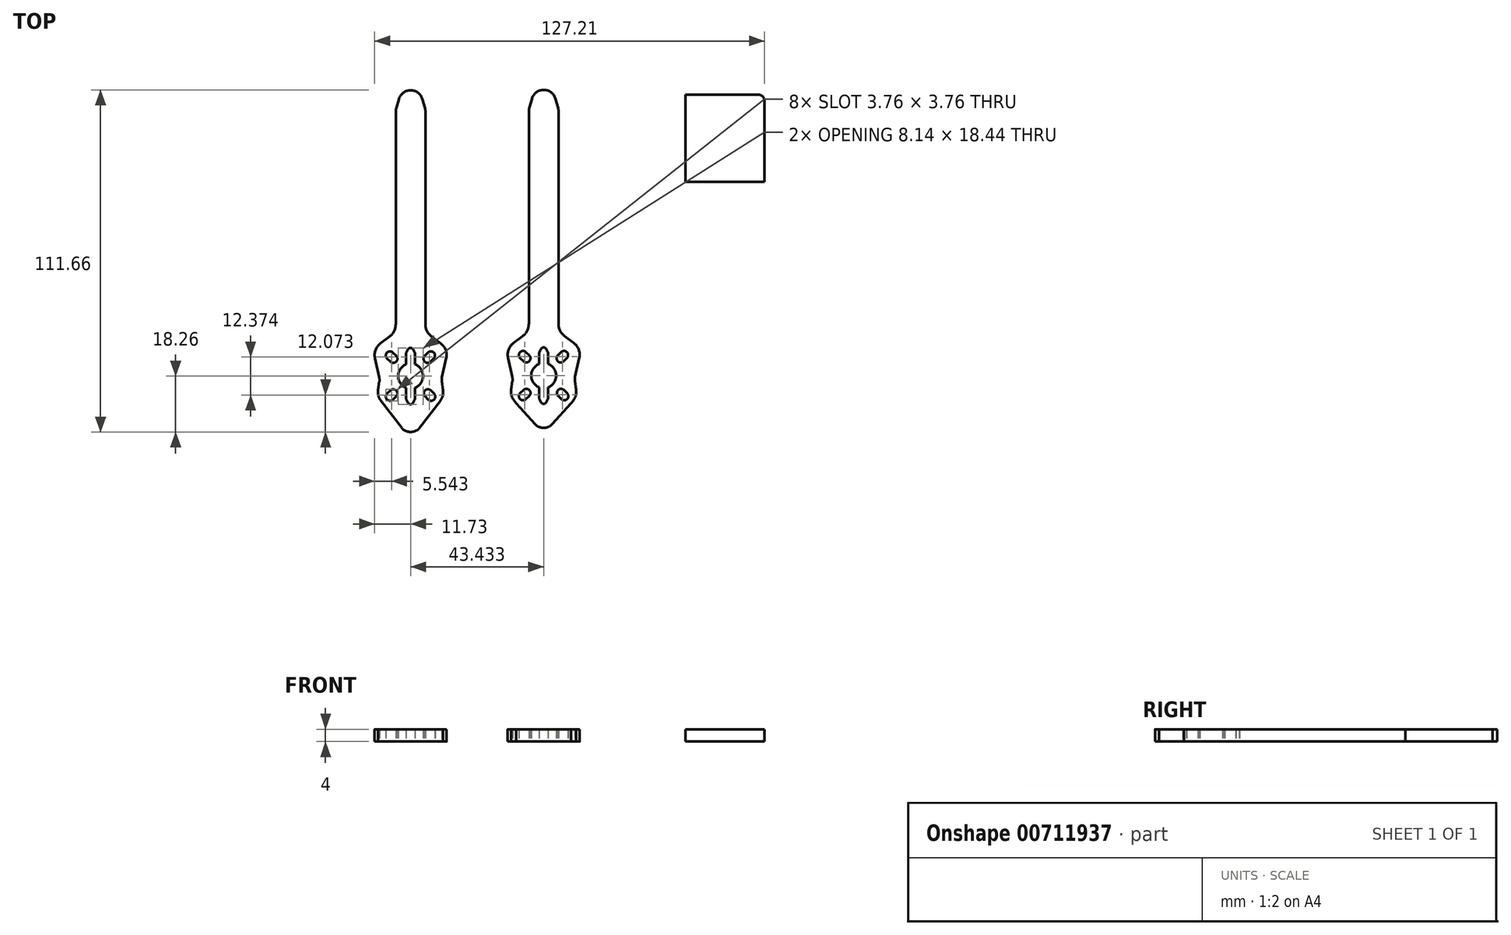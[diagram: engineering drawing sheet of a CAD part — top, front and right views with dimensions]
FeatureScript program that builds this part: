
annotation { "Feature Type Name" : "Feature", "Feature Type Description" : "" }
export const myFeature = defineFeature(function(context is Context, id is Id, definition is map)
    precondition{}
    {
        {
            var Q0;
            Q0=qCreatedBy(makeId("Top.planeOp"),FACE);
            var sketch = newSketch(context, id + "F0", { "sketchPlane" : qUnion([Q0])});
            skLineSegment(sketch, "E0", {"start": v(-0.1, -45.8) * mm, "end": v(-0.1, -63.2) * mm, "construction": true});
            skLineSegment(sketch, "E1", {"start": v(-0.1, -45.8) * mm, "end": v(-15.07, -60.77) * mm, "construction": true});
            skArc(sketch, "E2", {"start": v(-6.71, -41.1) * mm, "mid": v(-4.8, -41.1) * mm, "end": v(-4.8, -39.19) * mm});
            skArc(sketch, "E3", {"start": v(-5.86, -38.13) * mm, "mid": v(-7.77, -38.13) * mm, "end": v(-7.77, -40.04) * mm});
            skLineSegment(sketch, "E4", {"start": v(-4.8, -39.19) * mm, "end": v(-5.86, -38.13) * mm});
            skLineSegment(sketch, "E5.MirrorCS", {"start": v(-6.71, -41.1) * mm, "end": v(-7.77, -40.04) * mm});
            skLineSegment(sketch, "E6.MirrorCS", {"start": v(6.41, -41.1) * mm, "end": v(7.47, -40.04) * mm});
            skArc(sketch, "E7.MirrorCS", {"start": v(5.56, -38.13) * mm, "mid": v(7.47, -38.13) * mm, "end": v(7.47, -40.04) * mm});
            skLineSegment(sketch, "E8.MirrorCS", {"start": v(4.5, -39.19) * mm, "end": v(5.56, -38.13) * mm});
            skArc(sketch, "E9.MirrorCS", {"start": v(6.41, -41.1) * mm, "mid": v(4.5, -41.1) * mm, "end": v(4.5, -39.19) * mm});
            skLineSegment(sketch, "E10.MirrorCS", {"start": v(4.6, -52.41) * mm, "end": v(5.66, -53.47) * mm});
            skLineSegment(sketch, "E11.MirrorCS", {"start": v(6.51, -50.5) * mm, "end": v(7.57, -51.56) * mm});
            skArc(sketch, "E12.MirrorCS", {"start": v(6.51, -50.5) * mm, "mid": v(4.6, -50.5) * mm, "end": v(4.6, -52.41) * mm});
            skArc(sketch, "E13.MirrorCS", {"start": v(5.66, -53.47) * mm, "mid": v(7.57, -53.47) * mm, "end": v(7.57, -51.56) * mm});
            skLineSegment(sketch, "E14.MirrorCS", {"start": v(-4.8, -52.41) * mm, "end": v(-5.86, -53.47) * mm});
            skLineSegment(sketch, "E15.MirrorCS", {"start": v(-6.71, -50.5) * mm, "end": v(-7.77, -51.56) * mm});
            skArc(sketch, "E16.MirrorCS", {"start": v(-5.86, -53.47) * mm, "mid": v(-7.77, -53.47) * mm, "end": v(-7.77, -51.56) * mm});
            skArc(sketch, "E17.MirrorCS", {"start": v(-6.71, -50.5) * mm, "mid": v(-4.8, -50.5) * mm, "end": v(-4.8, -52.41) * mm});
            skLineSegment(sketch, "E18.left", {"start": v(1.4, -52.78) * mm, "end": v(1.4, -49.59) * mm});
            skLineSegment(sketch, "E18.right", {"start": v(-1.6, -52.78) * mm, "end": v(-1.6, -49.59) * mm});
            skLineSegment(sketch, "E19.trimOffspring", {"start": v(-1.6, -42.01) * mm, "end": v(-1.6, -38.82) * mm});
            skLineSegment(sketch, "E20.trimOffspring", {"start": v(1.4, -42.01) * mm, "end": v(1.4, -38.82) * mm});
            skArc(sketch, "E21.MirrorCS", {"start": v(-1.35, -37.85) * mm, "mid": v(-1.54, -38.32) * mm, "end": v(-1.6, -38.82) * mm});
            skArc(sketch, "E22.MirrorCS", {"start": v(1.4, -38.82) * mm, "mid": v(1.34, -38.32) * mm, "end": v(1.15, -37.85) * mm});
            skArc(sketch, "E23.MirrorCS", {"start": v(1.4, -52.78) * mm, "mid": v(1.34, -53.28) * mm, "end": v(1.15, -53.75) * mm});
            skArc(sketch, "E24.MirrorCS", {"start": v(-1.35, -53.75) * mm, "mid": v(-1.54, -53.28) * mm, "end": v(-1.6, -52.78) * mm});
            skCircle(sketch, "E25", {"center": v(-0.1, -45.8) * mm, "radius": 8 * mm, "construction": true});
            skLineSegment(sketch, "E26.MirrorCS", {"start": v(1.15, -37.85) * mm, "end": v(0.71, -37.06) * mm});
            skLineSegment(sketch, "E27.MirrorCS", {"start": v(-1.35, -37.85) * mm, "end": v(-0.91, -37.06) * mm});
            skArc(sketch, "E28.MirrorCS", {"start": v(-0.91, -37.06) * mm, "mid": v(-0.1, -36.58) * mm, "end": v(0.71, -37.06) * mm});
            skPoint(sketch, "E29.MirrorCS.start.orphan", {"position": v(-8.6, -37.25) * mm});
            skPoint(sketch, "E30.visualSharp", {"position": v(4.9, -63.2) * mm});
            skPoint(sketch, "E31.orphan", {"position": v(3.27, -64.64) * mm});
            skPoint(sketch, "E32", {"position": v(-0.1, -34.38) * mm});
            skPoint(sketch, "E33", {"position": v(-0.1, -36.58) * mm});
            skPoint(sketch, "E34", {"position": v(-0.1, -36.3) * mm});
            skArc(sketch, "E35", {"start": v(1.4, -49.59) * mm, "mid": v(3.97, -45.8) * mm, "end": v(1.4, -42.01) * mm});
            skArc(sketch, "E36.trimOffspring", {"start": v(-1.6, -42.01) * mm, "mid": v(-4.17, -45.8) * mm, "end": v(-1.6, -49.59) * mm});
            skPoint(sketch, "E37.MirrorP", {"position": v(-4.93, -29.8) * mm});
            skPoint(sketch, "E38.orphan", {"position": v(-8.46, -56.94) * mm});
            skPoint(sketch, "E39.visualSharp", {"position": v(-0.1, -65.3) * mm});
            skPoint(sketch, "E40.start.orphan", {"position": v(-2.37, -63.85) * mm});
            skPoint(sketch, "E41.orphan", {"position": v(2.17, -63.85) * mm});
            skPoint(sketch, "E42.orphan", {"position": v(6.78, -32.2) * mm});
            skPoint(sketch, "E43.MirrorCS.start.orphan", {"position": v(9.23, -33.3) * mm});
            skLineSegment(sketch, "E44", {"start": v(-0.1, -45.8) * mm, "end": v(1.26, -45.8) * mm, "construction": true});
            skLineSegment(sketch, "E45.MirrorCS", {"start": v(1.15, -53.75) * mm, "end": v(0.71, -54.54) * mm});
            skLineSegment(sketch, "E46.MirrorCS", {"start": v(-1.35, -53.75) * mm, "end": v(-0.91, -54.54) * mm});
            skArc(sketch, "E47.MirrorCS", {"start": v(-0.91, -54.54) * mm, "mid": v(-0.1, -55.02) * mm, "end": v(0.71, -54.54) * mm});
            skPoint(sketch, "E48.MirrorP", {"position": v(-12.53, -37.52) * mm});
            skLineSegment(sketch, "E49.MirrorCS", {"start": v(-9.87, -53.74) * mm, "end": v(-9.08, -54.78) * mm});
            skPoint(sketch, "E50.MirrorP", {"position": v(-9.3, -54.73) * mm});
            skLineSegment(sketch, "E51.MirrorCS", {"start": v(-10.67, -50.39) * mm, "end": v(-10.28, -47.6) * mm});
            skPoint(sketch, "E52.MirrorP", {"position": v(-11.56, -41.04) * mm});
            skPoint(sketch, "E53.MirrorP", {"position": v(-9.43, -33.3) * mm});
            skPoint(sketch, "E54.MirrorP", {"position": v(-8.6, -38.35) * mm});
            skPoint(sketch, "E55.MirrorP", {"position": v(-11.15, -41.7) * mm});
            skPoint(sketch, "E56.MirrorP", {"position": v(-10.73, -48.92) * mm});
            skLineSegment(sketch, "E57", {"start": v(-4.93, -28.16) * mm, "end": v(-4.93, -28.9) * mm});
            skPoint(sketch, "E58.end.orphan", {"position": v(-6.38, -32.73) * mm});
            skPoint(sketch, "E59.MirrorCS.end.orphan", {"position": v(6.18, -32.73) * mm});
            skPoint(sketch, "E60.visualSharp", {"position": v(-4.93, -31.43) * mm});
            skArc(sketch, "E60.filletArc", {"start": v(-6.98, -32.93) * mm, "mid": v(-5.47, -31.16) * mm, "end": v(-4.93, -28.9) * mm});
            skPoint(sketch, "E61.MirrorCS.end.orphan", {"position": v(-6.98, -32.2) * mm});
            skPoint(sketch, "E62.MirrorCS.end.orphan", {"position": v(4.73, -31.43) * mm});
            skArc(sketch, "E63.MirrorCS", {"start": v(6.78, -32.93) * mm, "mid": v(5.27, -31.16) * mm, "end": v(4.73, -28.9) * mm});
            skLineSegment(sketch, "E64.MirrorCS", {"start": v(4.73, -28.16) * mm, "end": v(4.73, -28.9) * mm});
            skLineSegment(sketch, "E65", {"start": v(-9.08, -54.78) * mm, "end": v(-2.91, -62.86) * mm});
            skArc(sketch, "E66", {"start": v(-2.52, -63.26) * mm, "mid": v(-0.1, -64.06) * mm, "end": v(2.32, -63.26) * mm});
            skPoint(sketch, "E67.orphan", {"position": v(-2.64, -63.23) * mm});
            skPoint(sketch, "E68.orphan", {"position": v(2.44, -63.23) * mm});
            skPoint(sketch, "E69.visualSharp", {"position": v(-2.77, -63.05) * mm});
            skArc(sketch, "E69.filletArc", {"start": v(-2.91, -62.86) * mm, "mid": v(-2.73, -63.07) * mm, "end": v(-2.52, -63.26) * mm});
            skPoint(sketch, "E70.visualSharp", {"position": v(2.57, -63.05) * mm});
            skArc(sketch, "E70.filletArc", {"start": v(2.32, -63.26) * mm, "mid": v(2.53, -63.07) * mm, "end": v(2.71, -62.86) * mm});
            skPoint(sketch, "E71.visualSharp", {"position": v(-12.78, -36.79) * mm});
            skLineSegment(sketch, "E72", {"start": v(-9.94, -35.14) * mm, "end": v(-6.98, -32.93) * mm});
            skLineSegment(sketch, "E73.MirrorCS", {"start": v(9.74, -35.14) * mm, "end": v(6.78, -32.93) * mm});
            skLineSegment(sketch, "E74", {"start": v(-4.93, -28.16) * mm, "end": v(-4.93, -23.9) * mm});
            skLineSegment(sketch, "E75.MirrorCS", {"start": v(4.73, -28.16) * mm, "end": v(4.73, -23.9) * mm});
            skLineSegment(sketch, "E76", {"start": v(-4.93, -23.9) * mm, "end": v(-4.93, 40.52) * mm});
            skLineSegment(sketch, "E77", {"start": v(4.73, -23.9) * mm, "end": v(4.73, 40.54) * mm});
            skLineSegment(sketch, "E78", {"start": v(4.59, 41.62) * mm, "end": v(3.77, 44.53) * mm});
            skLineSegment(sketch, "E79", {"start": v(-3.92, 44.58) * mm, "end": v(-4.77, 41.64) * mm});
            skPoint(sketch, "E80.visualSharp", {"position": v(0, 58.06) * mm});
            skArc(sketch, "E80.filletArc", {"start": v(3.77, 44.53) * mm, "mid": v(-0.06, 47.46) * mm, "end": v(-3.92, 44.58) * mm});
            skPoint(sketch, "E81.visualSharp", {"position": v(4.73, 41.1) * mm});
            skArc(sketch, "E81.filletArc", {"start": v(4.73, 40.54) * mm, "mid": v(4.7, 41.09) * mm, "end": v(4.59, 41.62) * mm});
            skPoint(sketch, "E82.visualSharp", {"position": v(-4.93, 41.1) * mm});
            skArc(sketch, "E82.filletArc", {"start": v(-4.77, 41.64) * mm, "mid": v(-4.9, 41.09) * mm, "end": v(-4.93, 40.52) * mm});
            skPoint(sketch, "E83", {"position": v(-10.67, -50.39) * mm});
            skPoint(sketch, "E84.visualSharp", {"position": v(-10.48, -52.95) * mm});
            skPoint(sketch, "E85", {"position": v(-10.18, -46.9) * mm});
            skPoint(sketch, "E86.MirrorCS.end.orphan", {"position": v(-10.04, -45.83) * mm});
            skPoint(sketch, "E86.MirrorCS.start.orphan", {"position": v(-10.17, -44.45) * mm});
            skPoint(sketch, "E87.start.orphan", {"position": v(-11.5, -40.54) * mm});
            skArc(sketch, "E88.filletArc", {"start": v(-10.28, -47.6) * mm, "mid": v(-10.25, -46.9) * mm, "end": v(-10.34, -46.2) * mm});
            skLineSegment(sketch, "E89.MirrorCS", {"start": v(8.88, -54.78) * mm, "end": v(2.71, -62.86) * mm});
            skArc(sketch, "E90.MirrorCS", {"start": v(10.08, -47.6) * mm, "mid": v(10.05, -46.9) * mm, "end": v(10.14, -46.2) * mm});
            skLineSegment(sketch, "E91.MirrorCS", {"start": v(11.52, -39.9) * mm, "end": v(10.14, -46.2) * mm});
            skArc(sketch, "E92", {"start": v(11.52, -39.9) * mm, "mid": v(11.33, -37.26) * mm, "end": v(9.74, -35.14) * mm});
            skPoint(sketch, "E71.filletArc.end.orphan", {"position": v(-11.72, -39.9) * mm});
            skArc(sketch, "E93.MirrorCS", {"start": v(-11.72, -39.9) * mm, "mid": v(-11.53, -37.26) * mm, "end": v(-9.94, -35.14) * mm});
            skLineSegment(sketch, "E94.MirrorCS", {"start": v(-11.72, -39.9) * mm, "end": v(-10.34, -46.2) * mm});
            skArc(sketch, "E95", {"start": v(-10.67, -50.39) * mm, "mid": v(-10.71, -51.37) * mm, "end": v(-10.56, -52.33) * mm});
            skPoint(sketch, "E96.visualSharp", {"position": v(-10.16, -53.36) * mm});
            skArc(sketch, "E96.filletArc", {"start": v(-10.56, -52.33) * mm, "mid": v(-10.28, -53.07) * mm, "end": v(-9.87, -53.74) * mm});
            skPoint(sketch, "E97.MirrorCS.end.orphan", {"position": v(8.88, -54.78) * mm});
            skArc(sketch, "E98.MirrorCS", {"start": v(10.36, -52.33) * mm, "mid": v(10.08, -53.07) * mm, "end": v(9.67, -53.74) * mm});
            skPoint(sketch, "E99.MirrorP", {"position": v(9.1, -54.73) * mm});
            skPoint(sketch, "E100.MirrorP", {"position": v(10.47, -50.39) * mm});
            skPoint(sketch, "E101.MirrorP", {"position": v(10.28, -52.95) * mm});
            skPoint(sketch, "E102.MirrorP", {"position": v(9.96, -53.36) * mm});
            skPoint(sketch, "E103.MirrorP", {"position": v(10.53, -48.92) * mm});
            skArc(sketch, "E104.MirrorCS", {"start": v(10.47, -50.39) * mm, "mid": v(10.51, -51.37) * mm, "end": v(10.36, -52.33) * mm});
            skLineSegment(sketch, "E105.MirrorCS", {"start": v(10.47, -50.39) * mm, "end": v(10.08, -47.6) * mm});
            skLineSegment(sketch, "E106.MirrorCS", {"start": v(9.67, -53.74) * mm, "end": v(8.88, -54.78) * mm});
            skLineSegment(sketch, "E107", {"start": v(-9.08, -54.78) * mm, "end": v(-2.87, -61.64) * mm});
            skLineSegment(sketch, "E108.MirrorCS", {"start": v(8.88, -54.78) * mm, "end": v(2.67, -61.64) * mm});
            skArc(sketch, "E109", {"start": v(-2.87, -61.64) * mm, "mid": v(-0.1, -62.86) * mm, "end": v(2.67, -61.64) * mm});
            skLineSegment(sketch, "E110", {"start": v(43.33, -45.66) * mm, "end": v(43.33, -63.05) * mm, "construction": true});
            skLineSegment(sketch, "E111", {"start": v(43.33, -45.66) * mm, "end": v(28.36, -60.63) * mm, "construction": true});
            skArc(sketch, "E112", {"start": v(36.72, -40.96) * mm, "mid": v(38.63, -40.96) * mm, "end": v(38.63, -39.05) * mm});
            skArc(sketch, "E113", {"start": v(37.57, -37.99) * mm, "mid": v(35.66, -37.99) * mm, "end": v(35.66, -39.9) * mm});
            skLineSegment(sketch, "E114", {"start": v(38.63, -39.05) * mm, "end": v(37.57, -37.99) * mm});
            skLineSegment(sketch, "E115.MirrorCS", {"start": v(36.72, -40.96) * mm, "end": v(35.66, -39.9) * mm});
            skLineSegment(sketch, "E116.MirrorCS", {"start": v(49.84, -40.96) * mm, "end": v(50.9, -39.9) * mm});
            skArc(sketch, "E117.MirrorCS", {"start": v(49, -37.99) * mm, "mid": v(50.9, -37.99) * mm, "end": v(50.9, -39.9) * mm});
            skLineSegment(sketch, "E118.MirrorCS", {"start": v(47.93, -39.05) * mm, "end": v(49, -37.99) * mm});
            skArc(sketch, "E119.MirrorCS", {"start": v(49.84, -40.96) * mm, "mid": v(47.93, -40.96) * mm, "end": v(47.93, -39.05) * mm});
            skLineSegment(sketch, "E120.MirrorCS", {"start": v(48.04, -52.27) * mm, "end": v(49.1, -53.33) * mm});
            skLineSegment(sketch, "E121.MirrorCS", {"start": v(49.94, -50.36) * mm, "end": v(51, -51.42) * mm});
            skArc(sketch, "E122.MirrorCS", {"start": v(49.94, -50.36) * mm, "mid": v(48.04, -50.36) * mm, "end": v(48.04, -52.27) * mm});
            skArc(sketch, "E123.MirrorCS", {"start": v(49.1, -53.33) * mm, "mid": v(51, -53.33) * mm, "end": v(51, -51.42) * mm});
            skLineSegment(sketch, "E124.MirrorCS", {"start": v(38.63, -52.27) * mm, "end": v(37.57, -53.33) * mm});
            skLineSegment(sketch, "E125.MirrorCS", {"start": v(36.72, -50.36) * mm, "end": v(35.66, -51.42) * mm});
            skArc(sketch, "E126.MirrorCS", {"start": v(37.57, -53.33) * mm, "mid": v(35.66, -53.33) * mm, "end": v(35.66, -51.42) * mm});
            skArc(sketch, "E127.MirrorCS", {"start": v(36.72, -50.36) * mm, "mid": v(38.63, -50.36) * mm, "end": v(38.63, -52.27) * mm});
            skLineSegment(sketch, "E128.left", {"start": v(44.83, -52.64) * mm, "end": v(44.83, -49.44) * mm});
            skLineSegment(sketch, "E128.right", {"start": v(41.83, -52.64) * mm, "end": v(41.83, -49.44) * mm});
            skLineSegment(sketch, "E129.trimOffspring", {"start": v(41.83, -41.87) * mm, "end": v(41.83, -38.68) * mm});
            skLineSegment(sketch, "E130.trimOffspring", {"start": v(44.83, -41.87) * mm, "end": v(44.83, -38.68) * mm});
            skArc(sketch, "E131.MirrorCS", {"start": v(42.08, -37.7) * mm, "mid": v(41.9, -38.17) * mm, "end": v(41.83, -38.68) * mm});
            skArc(sketch, "E132.MirrorCS", {"start": v(44.83, -38.68) * mm, "mid": v(44.77, -38.17) * mm, "end": v(44.58, -37.7) * mm});
            skArc(sketch, "E133.MirrorCS", {"start": v(44.83, -52.64) * mm, "mid": v(44.77, -53.14) * mm, "end": v(44.58, -53.61) * mm});
            skArc(sketch, "E134.MirrorCS", {"start": v(42.08, -53.61) * mm, "mid": v(41.9, -53.14) * mm, "end": v(41.83, -52.64) * mm});
            skCircle(sketch, "E135", {"center": v(43.33, -45.66) * mm, "radius": 8 * mm, "construction": true});
            skLineSegment(sketch, "E136.MirrorCS", {"start": v(44.58, -37.7) * mm, "end": v(44.15, -36.92) * mm});
            skLineSegment(sketch, "E137.MirrorCS", {"start": v(42.08, -37.7) * mm, "end": v(42.52, -36.92) * mm});
            skArc(sketch, "E138.MirrorCS", {"start": v(42.52, -36.92) * mm, "mid": v(43.33, -36.44) * mm, "end": v(44.15, -36.92) * mm});
            skPoint(sketch, "E139.MirrorCS.start.orphan", {"position": v(34.83, -37.11) * mm});
            skPoint(sketch, "E140.orphan", {"position": v(46.7, -64.5) * mm});
            skPoint(sketch, "E141", {"position": v(43.33, -34.24) * mm});
            skPoint(sketch, "E142", {"position": v(43.33, -36.44) * mm});
            skPoint(sketch, "E143", {"position": v(43.33, -36.16) * mm});
            skArc(sketch, "E144", {"start": v(44.83, -49.44) * mm, "mid": v(47.4, -45.66) * mm, "end": v(44.83, -41.87) * mm});
            skArc(sketch, "E145.trimOffspring", {"start": v(41.83, -41.87) * mm, "mid": v(39.26, -45.66) * mm, "end": v(41.83, -49.44) * mm});
            skPoint(sketch, "E146.MirrorP", {"position": v(38.5, -29.66) * mm});
            skPoint(sketch, "E147.orphan", {"position": v(34.98, -56.8) * mm});
            skPoint(sketch, "E148.visualSharp", {"position": v(43.33, -65.15) * mm});
            skPoint(sketch, "E149.orphan", {"position": v(50.22, -32.05) * mm});
            skPoint(sketch, "E150.MirrorCS.start.orphan", {"position": v(52.66, -33.17) * mm});
            skLineSegment(sketch, "E151", {"start": v(43.33, -45.66) * mm, "end": v(44.7, -45.66) * mm, "construction": true});
            skLineSegment(sketch, "E152.MirrorCS", {"start": v(44.58, -53.61) * mm, "end": v(44.15, -54.4) * mm});
            skLineSegment(sketch, "E153.MirrorCS", {"start": v(42.08, -53.61) * mm, "end": v(42.52, -54.4) * mm});
            skArc(sketch, "E154.MirrorCS", {"start": v(42.52, -54.4) * mm, "mid": v(43.33, -54.88) * mm, "end": v(44.15, -54.4) * mm});
            skPoint(sketch, "E155.MirrorP", {"position": v(30.9, -37.38) * mm});
            skLineSegment(sketch, "E156.MirrorCS", {"start": v(33.56, -53.6) * mm, "end": v(34.35, -54.64) * mm});
            skPoint(sketch, "E157.MirrorP", {"position": v(34.13, -54.59) * mm});
            skLineSegment(sketch, "E158.MirrorCS", {"start": v(32.76, -50.25) * mm, "end": v(33.15, -47.47) * mm});
            skPoint(sketch, "E159.MirrorP", {"position": v(31.87, -40.9) * mm});
            skPoint(sketch, "E160.MirrorP", {"position": v(34, -33.17) * mm});
            skPoint(sketch, "E161.MirrorP", {"position": v(34.83, -38.21) * mm});
            skPoint(sketch, "E162.MirrorP", {"position": v(32.28, -41.56) * mm});
            skPoint(sketch, "E163.MirrorP", {"position": v(32.7, -48.77) * mm});
            skLineSegment(sketch, "E164", {"start": v(38.5, -28.02) * mm, "end": v(38.5, -28.76) * mm});
            skPoint(sketch, "E165.end.orphan", {"position": v(37.05, -32.6) * mm});
            skPoint(sketch, "E166.MirrorCS.end.orphan", {"position": v(49.61, -32.6) * mm});
            skPoint(sketch, "E167.visualSharp", {"position": v(38.5, -31.3) * mm});
            skArc(sketch, "E167.filletArc", {"start": v(36.45, -32.8) * mm, "mid": v(37.96, -31.02) * mm, "end": v(38.5, -28.76) * mm});
            skPoint(sketch, "E168.MirrorCS.end.orphan", {"position": v(36.45, -32.05) * mm});
            skPoint(sketch, "E169.MirrorCS.end.orphan", {"position": v(48.17, -31.3) * mm});
            skArc(sketch, "E170.MirrorCS", {"start": v(50.21, -32.8) * mm, "mid": v(48.7, -31.02) * mm, "end": v(48.17, -28.76) * mm});
            skLineSegment(sketch, "E171.MirrorCS", {"start": v(48.17, -28.02) * mm, "end": v(48.17, -28.76) * mm});
            skPoint(sketch, "E172.visualSharp", {"position": v(30.65, -36.65) * mm});
            skLineSegment(sketch, "E173", {"start": v(33.5, -35) * mm, "end": v(36.45, -32.8) * mm});
            skLineSegment(sketch, "E174.MirrorCS", {"start": v(53.17, -35) * mm, "end": v(50.21, -32.8) * mm});
            skLineSegment(sketch, "E175", {"start": v(38.5, -28.02) * mm, "end": v(38.5, -23.77) * mm});
            skLineSegment(sketch, "E176.MirrorCS", {"start": v(48.17, -28.02) * mm, "end": v(48.17, -23.77) * mm});
            skLineSegment(sketch, "E177", {"start": v(38.5, -23.77) * mm, "end": v(38.5, 40.66) * mm});
            skLineSegment(sketch, "E178", {"start": v(48.17, -23.77) * mm, "end": v(48.17, 40.69) * mm});
            skLineSegment(sketch, "E179", {"start": v(48.02, 41.76) * mm, "end": v(47.2, 44.68) * mm});
            skLineSegment(sketch, "E180", {"start": v(39.51, 44.72) * mm, "end": v(38.66, 41.78) * mm});
            skPoint(sketch, "E181.visualSharp", {"position": v(43.43, 58.2) * mm});
            skArc(sketch, "E181.filletArc", {"start": v(47.2, 44.68) * mm, "mid": v(43.38, 47.6) * mm, "end": v(39.51, 44.72) * mm});
            skPoint(sketch, "E182.visualSharp", {"position": v(48.17, 41.23) * mm});
            skArc(sketch, "E182.filletArc", {"start": v(48.17, 40.69) * mm, "mid": v(48.13, 41.23) * mm, "end": v(48.02, 41.76) * mm});
            skPoint(sketch, "E183.visualSharp", {"position": v(38.5, 41.23) * mm});
            skArc(sketch, "E183.filletArc", {"start": v(38.66, 41.78) * mm, "mid": v(38.54, 41.23) * mm, "end": v(38.5, 40.66) * mm});
            skPoint(sketch, "E184", {"position": v(32.76, -50.25) * mm});
            skPoint(sketch, "E185.visualSharp", {"position": v(32.96, -52.8) * mm});
            skPoint(sketch, "E186", {"position": v(33.25, -46.76) * mm});
            skPoint(sketch, "E187.MirrorCS.end.orphan", {"position": v(33.4, -45.7) * mm});
            skPoint(sketch, "E187.MirrorCS.start.orphan", {"position": v(33.27, -44.3) * mm});
            skPoint(sketch, "E188.start.orphan", {"position": v(31.93, -40.4) * mm});
            skArc(sketch, "E189.filletArc", {"start": v(33.15, -47.47) * mm, "mid": v(33.19, -46.76) * mm, "end": v(33.1, -46.05) * mm});
            skArc(sketch, "E190.MirrorCS", {"start": v(53.52, -47.47) * mm, "mid": v(53.48, -46.76) * mm, "end": v(53.57, -46.05) * mm});
            skLineSegment(sketch, "E191.MirrorCS", {"start": v(54.95, -39.76) * mm, "end": v(53.57, -46.05) * mm});
            skArc(sketch, "E192", {"start": v(54.95, -39.76) * mm, "mid": v(54.77, -37.12) * mm, "end": v(53.17, -35) * mm});
            skPoint(sketch, "E172.filletArc.end.orphan", {"position": v(31.71, -39.76) * mm});
            skArc(sketch, "E193.MirrorCS", {"start": v(31.71, -39.76) * mm, "mid": v(31.9, -37.12) * mm, "end": v(33.5, -35) * mm});
            skLineSegment(sketch, "E194.MirrorCS", {"start": v(31.71, -39.76) * mm, "end": v(33.1, -46.05) * mm});
            skArc(sketch, "E195", {"start": v(32.76, -50.25) * mm, "mid": v(32.72, -51.22) * mm, "end": v(32.87, -52.19) * mm});
            skPoint(sketch, "E196.visualSharp", {"position": v(33.27, -53.22) * mm});
            skArc(sketch, "E196.filletArc", {"start": v(32.87, -52.19) * mm, "mid": v(33.15, -52.93) * mm, "end": v(33.56, -53.6) * mm});
            skPoint(sketch, "E197.MirrorCS.end.orphan", {"position": v(52.31, -54.64) * mm});
            skArc(sketch, "E198.MirrorCS", {"start": v(53.8, -52.19) * mm, "mid": v(53.52, -52.93) * mm, "end": v(53.1, -53.6) * mm});
            skPoint(sketch, "E199.MirrorP", {"position": v(52.54, -54.59) * mm});
            skPoint(sketch, "E200.MirrorP", {"position": v(53.9, -50.25) * mm});
            skPoint(sketch, "E201.MirrorP", {"position": v(53.7, -52.8) * mm});
            skPoint(sketch, "E202.MirrorP", {"position": v(53.4, -53.22) * mm});
            skPoint(sketch, "E203.MirrorP", {"position": v(53.96, -48.77) * mm});
            skArc(sketch, "E204.MirrorCS", {"start": v(53.9, -50.25) * mm, "mid": v(53.95, -51.22) * mm, "end": v(53.8, -52.19) * mm});
            skLineSegment(sketch, "E205.MirrorCS", {"start": v(53.9, -50.25) * mm, "end": v(53.52, -47.47) * mm});
            skLineSegment(sketch, "E206.MirrorCS", {"start": v(53.1, -53.6) * mm, "end": v(52.31, -54.64) * mm});
            skLineSegment(sketch, "E207", {"start": v(34.35, -54.64) * mm, "end": v(40.57, -61.5) * mm});
            skLineSegment(sketch, "E208.MirrorCS", {"start": v(52.31, -54.64) * mm, "end": v(46.1, -61.5) * mm});
            skArc(sketch, "E209", {"start": v(40.57, -61.5) * mm, "mid": v(43.33, -62.72) * mm, "end": v(46.1, -61.5) * mm});
            skPoint(sketch, "E210.start.orphan", {"position": v(34.35, -54.64) * mm});
            skLineSegment(sketch, "E211.bottom", {"start": v(89.65, 46.07) * mm, "end": v(113.38, 46.07) * mm});
            skLineSegment(sketch, "E211.top", {"start": v(89.65, 17.64) * mm, "end": v(115.38, 17.64) * mm});
            skLineSegment(sketch, "E211.left", {"start": v(89.65, 46.07) * mm, "end": v(89.65, 17.64) * mm});
            skLineSegment(sketch, "E211.right", {"start": v(115.38, 44.07) * mm, "end": v(115.38, 17.64) * mm});
            skPoint(sketch, "E212.visualSharp", {"position": v(115.38, 46.07) * mm});
            skArc(sketch, "E212.filletArc", {"start": v(115.38, 44.07) * mm, "mid": v(114.8, 45.48) * mm, "end": v(113.38, 46.07) * mm});
            skSolve(sketch);
        }
        {
            var Q0;
            Q0 = qSketchRegion(id + "F0", true);
            extrude(context, id + "F1", {"entities" : qUnion([Q0]), "depth" : 4 * mm, "offsetDistance" : 25 * mm});
        }
    });
